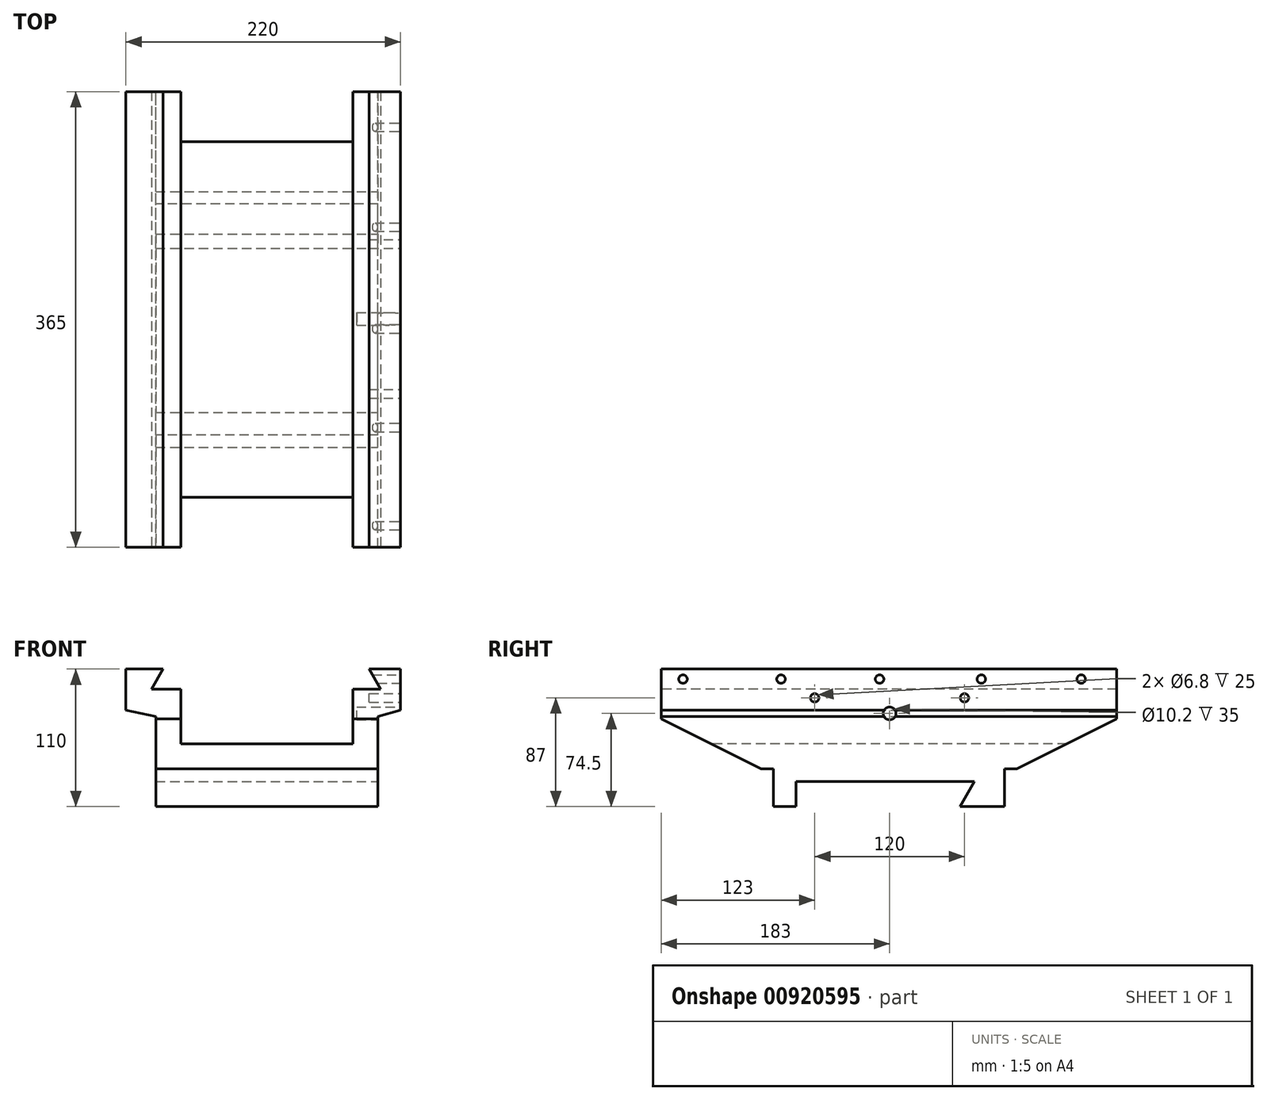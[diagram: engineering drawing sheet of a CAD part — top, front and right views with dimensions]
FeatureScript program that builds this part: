
annotation { "Feature Type Name" : "Feature", "Feature Type Description" : "" }
export const myFeature = defineFeature(function(context is Context, id is Id, definition is map)
    precondition{}
    {
        {
            var Q0;
            Q0=qCreatedBy(makeId("Front.planeOp"),FACE);
            var sketch = newSketch(context, id + "F0", { "sketchPlane" : qUnion([Q0])});
            skLineSegment(sketch, "E0", {"start": v(-110, 0) * mm, "end": v(110, 0) * mm});
            skLineSegment(sketch, "E1", {"start": v(110, 0) * mm, "end": v(110, -33) * mm});
            skLineSegment(sketch, "E2", {"start": v(92, -38) * mm, "end": v(92, -110) * mm});
            skLineSegment(sketch, "E3", {"start": v(92, -110) * mm, "end": v(-86, -110) * mm});
            skLineSegment(sketch, "E4", {"start": v(-86, -110) * mm, "end": v(-86, -38) * mm});
            skLineSegment(sketch, "E5", {"start": v(-110, 0) * mm, "end": v(-110, -33) * mm});
            skLineSegment(sketch, "E6", {"start": v(-110, -33) * mm, "end": v(-86, -38) * mm});
            skLineSegment(sketch, "E7", {"start": v(110, -33) * mm, "end": v(92, -38) * mm});
            skSolve(sketch);
        }
        {
            var Q0;
            Q0=makeQuery(id+"F0.imprint","IMPRINT",FACE,{"disambiguationData":[TD([[makeQuery(id+"F0.imprint","IMPRINT",EDGE,{"derivedFrom":sQuery(id+"F0.wireOp",EDGE,"E0")}),-1.0]])]});
            extrude(context, id + "F1", {"entities" : qUnion([Q0]), "depth" : 365 * mm, "offsetDistance" : 25 * mm, "symmetric" : true});
        }
        {
            var Q0;
            Q0=qCreatedBy(makeId("Front.planeOp"),FACE);
            var sketch = newSketch(context, id + "F2", { "sketchPlane" : qUnion([Q0])});
            skLineSegment(sketch, "E8", {"start": v(-80.34, 0) * mm, "end": v(84.96, 0) * mm});
            skLineSegment(sketch, "E9", {"start": v(84.96, 0) * mm, "end": v(94.2, -16) * mm});
            skLineSegment(sketch, "E10", {"start": v(94.2, -16) * mm, "end": v(-89.58, -16) * mm});
            skLineSegment(sketch, "E11", {"start": v(-89.58, -16) * mm, "end": v(-80.34, 0) * mm});
            skLineSegment(sketch, "E12", {"start": v(-89.58, -16) * mm, "end": v(89.58, -16) * mm, "construction": true});
            skLineSegment(sketch, "E13", {"start": v(89.58, -16) * mm, "end": v(80.34, 0) * mm, "construction": true});
            skLineSegment(sketch, "E14", {"start": v(80.34, 0) * mm, "end": v(-80.34, 0) * mm, "construction": true});
            skLineSegment(sketch, "E15", {"start": v(-89, -15) * mm, "end": v(89, -15) * mm, "construction": true});
            skSolve(sketch);
        }
        {
            var Q0;
            Q0=makeQuery(id+"F2.imprint","IMPRINT",FACE,{"disambiguationData":[TD([[makeQuery(id+"F2.imprint","IMPRINT",EDGE,{"derivedFrom":sQuery(id+"F2.wireOp",EDGE,"E11")}),-1.0]])]});
            extrude(context, id + "F3", {"entities" : qUnion([Q0]), "operationType" : NewBodyOperationType.REMOVE, "oppositeDirection" : true, "depth" : 400 * mm, "offsetDistance" : 25 * mm, "symmetric" : true});
        }
        {
            var Q0;
            Q0=qCreatedBy(makeId("Right.planeOp"),FACE);
            var sketch = newSketch(context, id + "F4", { "sketchPlane" : qUnion([Q0])});
            skLineSegment(sketch, "E16.0", {"start": v(-182.5, -110) * mm, "end": v(182.5, -110) * mm, "construction": true});
            skLineSegment(sketch, "E17", {"start": v(-74.5, -110) * mm, "end": v(-74.5, -90) * mm});
            skLineSegment(sketch, "E18", {"start": v(-74.5, -90) * mm, "end": v(68.5, -90) * mm});
            skLineSegment(sketch, "E19", {"start": v(68.5, -90) * mm, "end": v(56.95, -110) * mm});
            skLineSegment(sketch, "E20", {"start": v(56.95, -110) * mm, "end": v(-74.5, -110) * mm});
            skSolve(sketch);
        }
        {
            var Q0;
            Q0=makeQuery(id+"F4.imprint","IMPRINT",FACE,{"disambiguationData":[TD([[makeQuery(id+"F4.imprint","IMPRINT",EDGE,{"derivedFrom":sQuery(id+"F4.wireOp",EDGE,"E17")}),-1.0]])]});
            extrude(context, id + "F5", {"entities" : qUnion([Q0]), "operationType" : NewBodyOperationType.REMOVE, "oppositeDirection" : true, "depth" : 400 * mm, "offsetDistance" : 25 * mm, "symmetric" : true});
        }
        {
            var Q0;
            Q0=makeQuery(id+"F1.opExtrude","SWEPT_FACE",FACE,{"disambiguationData":[OSD([sQuery(id+"F0.wireOp",EDGE,"E1")])]});
            var sketch = newSketch(context, id + "F6", { "sketchPlane" : qUnion([Q0])});
            skLineSegment(sketch, "E21", {"start": v(-182.5, -40) * mm, "end": v(-102.5, -80) * mm});
            skLineSegment(sketch, "E22", {"start": v(-102.5, -80) * mm, "end": v(-92.5, -80) * mm});
            skLineSegment(sketch, "E23", {"start": v(-92.5, -80) * mm, "end": v(-92.5, -150) * mm});
            skLineSegment(sketch, "E24", {"start": v(-92.5, -150) * mm, "end": v(-182.5, -150) * mm});
            skLineSegment(sketch, "E25", {"start": v(-182.5, -150) * mm, "end": v(-182.5, -40) * mm});
            skLineSegment(sketch, "E26", {"start": v(182.5, -40) * mm, "end": v(102.5, -80) * mm});
            skLineSegment(sketch, "E27", {"start": v(102.5, -80) * mm, "end": v(92.5, -80) * mm});
            skLineSegment(sketch, "E28", {"start": v(92.5, -80) * mm, "end": v(92.5, -150) * mm});
            skLineSegment(sketch, "E29", {"start": v(92.5, -150) * mm, "end": v(182.5, -150) * mm});
            skLineSegment(sketch, "E30", {"start": v(182.5, -150) * mm, "end": v(182.5, -40) * mm});
            skSolve(sketch);
        }
        {
            var Q0;
            Q0=makeQuery(id+"F6.imprint","IMPRINT",FACE,{"disambiguationData":[TD([[makeQuery(id+"F6.imprint","IMPRINT",EDGE,{"derivedFrom":sQuery(id+"F6.wireOp",EDGE,"E21")}),-1.0]])]});
            var Q1;
            Q1=makeQuery(id+"F6.imprint","IMPRINT",FACE,{"disambiguationData":[TD([[makeQuery(id+"F6.imprint","IMPRINT",EDGE,{"derivedFrom":sQuery(id+"F6.wireOp",EDGE,"E26")}),1.0]])]});
            extrude(context, id + "F7", {"entities" : qUnion([Q0, Q1]), "operationType" : NewBodyOperationType.REMOVE, "endBound" : BoundingType.THROUGH_ALL, "oppositeDirection" : true, "depth" : 25 * mm, "offsetDistance" : 25 * mm});
        }
        {
            var Q0;
            Q0=makeQuery(id+"F1.opExtrude","CAP_FACE",FACE,{"disambiguationData":[OSD([sQuery(id+"F0.wireOp",EDGE,"E0"),sQuery(id+"F0.wireOp",EDGE,"E1"),sQuery(id+"F0.wireOp",EDGE,"E2"),sQuery(id+"F0.wireOp",EDGE,"E3"),sQuery(id+"F0.wireOp",EDGE,"E4"),sQuery(id+"F0.wireOp",EDGE,"E5"),sQuery(id+"F0.wireOp",EDGE,"E6"),sQuery(id+"F0.wireOp",EDGE,"E7")])],"isStart":false});
            var sketch = newSketch(context, id + "F8", { "sketchPlane" : qUnion([Q0])});
            skLineSegment(sketch, "E31.bottom", {"start": v(-66, -16) * mm, "end": v(72, -16) * mm});
            skLineSegment(sketch, "E31.top", {"start": v(-66, -60) * mm, "end": v(72, -60) * mm});
            skLineSegment(sketch, "E31.left", {"start": v(-66, -16) * mm, "end": v(-66, -60) * mm});
            skLineSegment(sketch, "E31.right", {"start": v(72, -16) * mm, "end": v(72, -60) * mm});
            skSolve(sketch);
        }
        {
            var Q0;
            {var subQ0=sQuery(id+"F8.wireOp",EDGE,"E31.top");Q0=makeQuery(id+"F8.imprint","IMPRINT",FACE,{"disambiguationData":[TD([[makeQuery(id+"F8.imprint","IMPRINT",EDGE,{"derivedFrom":subQ0}),1.0]])]});}
            var Q1;
            {var subQ0=sQuery(id+"F8.wireOp",EDGE,"E31.bottom");Q1=makeQuery(id+"F8.imprint","IMPRINT",FACE,{"disambiguationData":[TD([[makeQuery(id+"F8.imprint","IMPRINT",EDGE,{"derivedFrom":subQ0}),1.0]])]});}
            extrude(context, id + "F9", {"entities" : qUnion([Q0, Q1]), "operationType" : NewBodyOperationType.REMOVE, "endBound" : BoundingType.THROUGH_ALL, "oppositeDirection" : true, "depth" : 25 * mm, "offsetDistance" : 25 * mm});
        }
        {
            var Q0;
            Q0=makeQuery(id+"F1.opExtrude","SWEPT_FACE",FACE,{"disambiguationData":[OSD([sQuery(id+"F0.wireOp",EDGE,"E1")])]});
            var sketch = newSketch(context, id + "F10", { "sketchPlane" : qUnion([Q0])});
            skCircle(sketch, "E32", {"center": v(-165, -8) * mm, "radius": 3.4 * mm});
            skCircle(sketch, "E33", {"center": v(-86.5, -8) * mm, "radius": 3.4 * mm});
            skCircle(sketch, "E34", {"center": v(-7.5, -8) * mm, "radius": 3.4 * mm});
            skCircle(sketch, "E35", {"center": v(74, -8) * mm, "radius": 3.4 * mm});
            skCircle(sketch, "E36", {"center": v(154, -8) * mm, "radius": 3.4 * mm});
            skSolve(sketch);
        }
        {
            var Q0;
            Q0=makeQuery(id+"F1.opExtrude","SWEPT_FACE",FACE,{"disambiguationData":[OSD([sQuery(id+"F0.wireOp",EDGE,"E1")])]});
            var sketch = newSketch(context, id + "F11", { "sketchPlane" : qUnion([Q0])});
            skCircle(sketch, "E37", {"center": v(0.5, -35.5) * mm, "radius": 5.1 * mm});
            skSolve(sketch);
        }
        {
            var Q0;
            {var subQ0=sQuery(id+"F11.wireOp",EDGE,"E37");var subQ1=makeQuery(id+"F1.opExtrude","SWEPT_EDGE",EDGE,{"disambiguationData":[OSD([sQuery(id+"F0.wireOp",EDGE,"E1"),sQuery(id+"F0.wireOp",EDGE,"E7")])]});var subQ2=makeQuery(id+"F11.imprint","INTERSECT",VERTEX,{"disambiguationData":[OD(0.0)],"derivedFrom":[subQ1,subQ0]});Q0=makeQuery(id+"F11.imprint","IMPRINT",FACE,{"disambiguationData":[TD([[makeQuery(id+"F11.imprint","IMPRINT",EDGE,{"disambiguationData":[TD([[subQ2,1.0]])],"derivedFrom":subQ0}),1.0]])]});}
            var Q1;
            {var subQ0=sQuery(id+"F11.wireOp",EDGE,"E37");var subQ1=makeQuery(id+"F1.opExtrude","SWEPT_EDGE",EDGE,{"disambiguationData":[OSD([sQuery(id+"F0.wireOp",EDGE,"E1"),sQuery(id+"F0.wireOp",EDGE,"E7")])]});var subQ2=makeQuery(id+"F11.imprint","INTERSECT",VERTEX,{"disambiguationData":[OD(0.0)],"derivedFrom":[subQ1,subQ0]});Q1=makeQuery(id+"F11.imprint","IMPRINT",FACE,{"disambiguationData":[TD([[makeQuery(id+"F11.imprint","IMPRINT",EDGE,{"disambiguationData":[TD([[subQ2,-1.0]])],"derivedFrom":subQ0}),1.0]])]});}
            extrude(context, id + "F12", {"entities" : qUnion([Q0, Q1]), "operationType" : NewBodyOperationType.REMOVE, "oppositeDirection" : true, "depth" : 35 * mm, "offsetDistance" : 25 * mm});
        }
        {
            var Q0;
            Q0=makeQuery(id+"F1.opExtrude","SWEPT_FACE",FACE,{"disambiguationData":[OSD([sQuery(id+"F0.wireOp",EDGE,"E1")])]});
            var sketch = newSketch(context, id + "F13", { "sketchPlane" : qUnion([Q0])});
            skCircle(sketch, "E38", {"center": v(-59.5, -23) * mm, "radius": 3.4 * mm});
            skCircle(sketch, "E39", {"center": v(60.5, -23) * mm, "radius": 3.4 * mm});
            skSolve(sketch);
        }
        {
            var Q0;
            Q0=makeQuery(id+"F10.imprint","IMPRINT",FACE,{"disambiguationData":[TD([[makeQuery(id+"F10.imprint","IMPRINT",EDGE,{"derivedFrom":sQuery(id+"F10.wireOp",EDGE,"E32")}),1.0]])]});
            var Q1;
            Q1=makeQuery(id+"F10.imprint","IMPRINT",FACE,{"disambiguationData":[TD([[makeQuery(id+"F10.imprint","IMPRINT",EDGE,{"derivedFrom":sQuery(id+"F10.wireOp",EDGE,"E33")}),1.0]])]});
            var Q2;
            Q2=makeQuery(id+"F10.imprint","IMPRINT",FACE,{"disambiguationData":[TD([[makeQuery(id+"F10.imprint","IMPRINT",EDGE,{"derivedFrom":sQuery(id+"F10.wireOp",EDGE,"E34")}),1.0]])]});
            var Q3;
            Q3=makeQuery(id+"F10.imprint","IMPRINT",FACE,{"disambiguationData":[TD([[makeQuery(id+"F10.imprint","IMPRINT",EDGE,{"derivedFrom":sQuery(id+"F10.wireOp",EDGE,"E35")}),1.0]])]});
            var Q4;
            Q4=makeQuery(id+"F10.imprint","IMPRINT",FACE,{"disambiguationData":[TD([[makeQuery(id+"F10.imprint","IMPRINT",EDGE,{"derivedFrom":sQuery(id+"F10.wireOp",EDGE,"E36")}),1.0]])]});
            extrude(context, id + "F14", {"entities" : qUnion([Q0, Q1, Q2, Q3, Q4]), "operationType" : NewBodyOperationType.REMOVE, "endBound" : BoundingType.UP_TO_NEXT, "oppositeDirection" : true, "depth" : 25 * mm, "offsetDistance" : 25 * mm});
        }
        {
            var Q0;
            Q0=makeQuery(id+"F13.imprint","IMPRINT",FACE,{"disambiguationData":[TD([[makeQuery(id+"F13.imprint","IMPRINT",EDGE,{"derivedFrom":sQuery(id+"F13.wireOp",EDGE,"E38")}),1.0]])]});
            var Q1;
            Q1=makeQuery(id+"F13.imprint","IMPRINT",FACE,{"disambiguationData":[TD([[makeQuery(id+"F13.imprint","IMPRINT",EDGE,{"derivedFrom":sQuery(id+"F13.wireOp",EDGE,"E39")}),1.0]])]});
            extrude(context, id + "F15", {"entities" : qUnion([Q0, Q1]), "operationType" : NewBodyOperationType.REMOVE, "oppositeDirection" : true, "depth" : 25 * mm, "offsetDistance" : 25 * mm});
        }
        {
            var Q0;
            Q0=makeQuery(id+"F13.imprint","IMPRINT",FACE,{"disambiguationData":[TD([[makeQuery(id+"F13.imprint","IMPRINT",EDGE,{"derivedFrom":sQuery(id+"F13.wireOp",EDGE,"E38")}),1.0]])]});
            var Q1;
            Q1=makeQuery(id+"F13.imprint","IMPRINT",FACE,{"disambiguationData":[TD([[makeQuery(id+"F13.imprint","IMPRINT",EDGE,{"derivedFrom":sQuery(id+"F13.wireOp",EDGE,"E39")}),1.0]])]});
            extrude(context, id + "F16", {"entities" : qUnion([Q0, Q1]), "operationType" : NewBodyOperationType.REMOVE, "oppositeDirection" : true, "depth" : 25 * mm, "offsetDistance" : 25 * mm});
        }
    });
